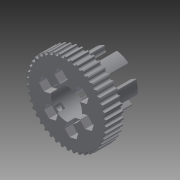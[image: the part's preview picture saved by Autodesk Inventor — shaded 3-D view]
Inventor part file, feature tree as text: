
AUTODESK INVENTOR PART (.ipt)
format: ipt  version: 2015 (Build 190159000, 159)  size: 2,182,144 bytes
history: native  units: in
note: dims shown in document units (in); Inventor stores cm internally (conversion verified against a paired STEP export)
features: reference x15, extrude x6, sketch x6, fillet x6, chamfer x2, plane x1, hole x1, pattern_circular x1
ambient origin geometry x8: Origin, YZ Plane, XZ Plane, XY Plane, X Axis, Y Axis, Z Axis, Center Point
bodies: Solid1 (feature_tree)
feature tree (38):
  extrude  "Pulley"  Depth=0.22in TaperAngle=0.0deg
  extrude  "Spacer"  Depth=0.58in TaperAngle=0.0deg
  chamfer  "Chamfer1"  [1 undecoded]
  extrude  "Spoke"  Depth=0.04in
  extrude  "Center Hole"  Depth=0.009in
  plane  "Work Plane3"
  extrude  "Pulley Center Cutout"  Depth=0.009in TaperAngle=0.0deg
  chamfer  "Chamfer2"  Distance=2.3622in Angle=360.0deg
  sketch  "Sketch10"  dims[d37=1.0in d38=1.0in d39=0.225in d40=0.75in d41=0.375in d42=0.25in d43=0.5635in d44=1.0in d45=0.8108in d46=0.395in d47=0.25in d48=0.0in d49=2.3622in d50=360.0deg d65=0.02in d66=0.02in d68=0.078in d69=0.009in d71=0.025in d72=0.01in d73=-0.1in]
  hole  "Hole1"  [1 undecoded]
  extrude  "Nut Pocket"  Depth=0.009in
  fillet  "Fillet7"  Radius=0.078in
  fillet  "Fillet8"  Radius=0.009in
  fillet  "Fillet9"  Radius=0.025in
  fillet  "Fillet10"  Radius=0.01in
  fillet  "Fillet11"  [1 undecoded]
  pattern_circular  "Circular Pattern3"  [2 undecoded]
  fillet  "Fillet3"  [1 undecoded]
  sketch  "Sketch1"  dims[d0=0.5512in d1=0.0in d2=0.22in d3=0.0in]
  reference  "Reference1"
  sketch  "Sketch2"  dims[d4=0.35in d5=0.22in d6=45.0deg d12=0.58in d13=0.0in]
  sketch  "Sketch5"  dims[d14=1.3in d15=0.0in d16=0.0in]
  sketch  "Sketch6"  dims[d17=0.25in d18=0.1in d19=45.0deg d32=0.04in]
  sketch  "Sketch9"  dims[d35=0.75in d36=0.0in]
  reference  "Reference40"
  reference  "Reference41"
  reference  "Reference42"
  reference  "Reference43"
  reference  "Reference44"
  reference  "Reference45"
  reference  "Reference46"
  reference  "Reference47"
  reference  "Reference48"
  reference  "Reference49"
  reference  "Reference50"
  reference  "Reference51"
  reference  "Reference52"
  reference  "Reference53"
note: 6 required parameter values undecoded (feature->parameter linkage not recoverable at this tier; creation-order binding heuristic only, values carry confidence <= 0.55)
